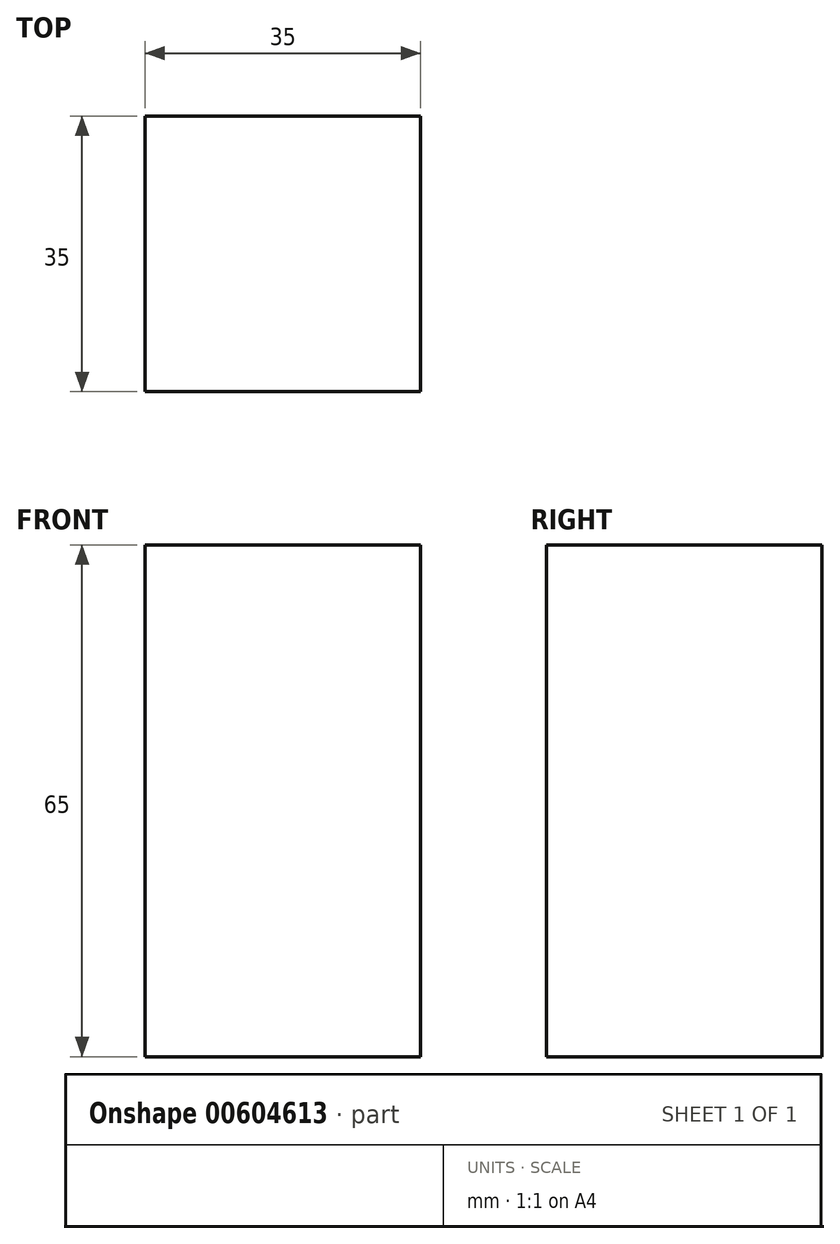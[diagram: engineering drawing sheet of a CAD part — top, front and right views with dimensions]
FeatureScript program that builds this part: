
annotation { "Feature Type Name" : "Feature", "Feature Type Description" : "" }
export const myFeature = defineFeature(function(context is Context, id is Id, definition is map)
    precondition{}
    {
        {
            var Q0;
            Q0=qCreatedBy(makeId("Top.planeOp"),FACE);
            var sketch = newSketch(context, id + "F0", { "sketchPlane" : qUnion([Q0])});
            skLineSegment(sketch, "E0.bottom", {"start": v(-16.78, -14.17) * mm, "end": v(18.22, -14.17) * mm});
            skLineSegment(sketch, "E0.top", {"start": v(-16.78, 20.83) * mm, "end": v(18.22, 20.83) * mm});
            skLineSegment(sketch, "E0.left", {"start": v(-16.78, -14.17) * mm, "end": v(-16.78, 20.83) * mm});
            skLineSegment(sketch, "E0.right", {"start": v(18.22, -14.17) * mm, "end": v(18.22, 20.83) * mm});
            skSolve(sketch);
        }
        {
            var Q0;
            Q0 = qSketchRegion(id + "F0", true);
            extrude(context, id + "F1", {"entities" : qUnion([Q0]), "depth" : 65 * mm, "offsetDistance" : 25.4 * mm});
        }
    });
